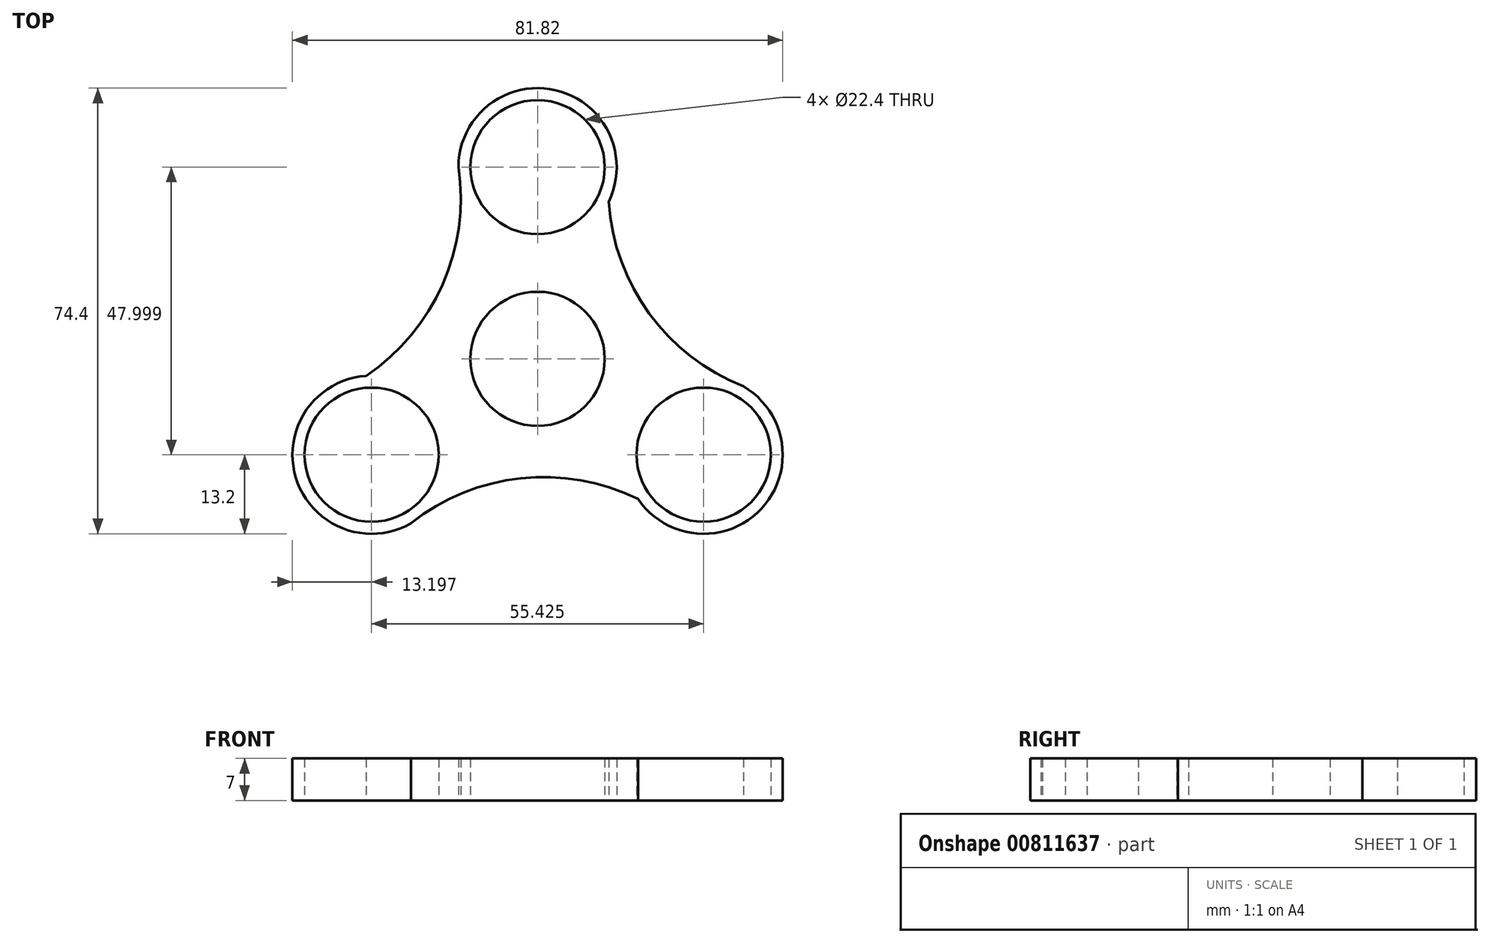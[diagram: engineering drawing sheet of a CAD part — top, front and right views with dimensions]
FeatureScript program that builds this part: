
annotation { "Feature Type Name" : "Feature", "Feature Type Description" : "" }
export const myFeature = defineFeature(function(context is Context, id is Id, definition is map)
    precondition{}
    {
        {
            var Q0;
            Q0=qCreatedBy(makeId("Top.planeOp"),FACE);
            var sketch = newSketch(context, id + "F0", { "sketchPlane" : qUnion([Q0])});
            skCircle(sketch, "E0", {"center": v(0, 0) * mm, "radius": 11.2 * mm});
            skCircle(sketch, "E1", {"center": v(0, 32) * mm, "radius": 11.2 * mm});
            skCircle(sketch, "E2", {"center": v(0, 0) * mm, "radius": 13.2 * mm});
            skCircle(sketch, "E3", {"center": v(0, 32) * mm, "radius": 13.2 * mm});
            skCircle(sketch, "E4.1.0", {"center": v(-27.71, -16) * mm, "radius": 11.2 * mm});
            skCircle(sketch, "E4.1.1", {"center": v(-27.71, -16) * mm, "radius": 13.2 * mm});
            skCircle(sketch, "E4.2.0", {"center": v(27.71, -16) * mm, "radius": 11.2 * mm});
            skCircle(sketch, "E4.2.1", {"center": v(27.71, -16) * mm, "radius": 13.2 * mm});
            skArc(sketch, "E5", {"start": v(-28.63, -2.83) * mm, "mid": v(-15.87, 12.38) * mm, "end": v(-13.2, 32.04) * mm});
            skLineSegment(sketch, "E6", {"start": v(-15.87, 12.38) * mm, "end": v(-9.94, 8.68) * mm});
            skLineSegment(sketch, "E7", {"start": v(-17.08, 9.91) * mm, "end": v(-11.67, 6.17) * mm});
            skArc(sketch, "E8.1.0", {"start": v(16.76, -23.37) * mm, "mid": v(-2.78, -19.93) * mm, "end": v(-21.15, -27.45) * mm});
            skLineSegment(sketch, "E8.1.1", {"start": v(-2.78, -19.93) * mm, "end": v(-2.55, -12.95) * mm});
            skLineSegment(sketch, "E8.1.2", {"start": v(-0.04, -19.75) * mm, "end": v(0.49, -13.2) * mm});
            skArc(sketch, "E8.2.0", {"start": v(11.86, 26.2) * mm, "mid": v(18.65, 7.56) * mm, "end": v(34.35, -4.59) * mm});
            skLineSegment(sketch, "E8.2.1", {"start": v(18.65, 7.56) * mm, "end": v(12.5, 4.27) * mm});
            skLineSegment(sketch, "E8.2.2", {"start": v(17.12, 9.84) * mm, "end": v(11.18, 7.02) * mm});
            skSolve(sketch);
        }
        {
            var Q0;
            Q0=makeQuery(id+"F0.imprint","IMPRINT",FACE,{"disambiguationData":[TD([[makeQuery(id+"F0.imprint","IMPRINT",EDGE,{"derivedFrom":sQuery(id+"F0.wireOp",EDGE,"E1")}),-1.0]])]});
            var Q1;
            Q1=makeQuery(id+"F0.imprint","IMPRINT",FACE,{"disambiguationData":[TD([[makeQuery(id+"F0.imprint","IMPRINT",EDGE,{"derivedFrom":sQuery(id+"F0.wireOp",EDGE,"E4.1.0")}),-1.0]])]});
            var Q2;
            Q2=makeQuery(id+"F0.imprint","IMPRINT",FACE,{"disambiguationData":[TD([[makeQuery(id+"F0.imprint","IMPRINT",EDGE,{"derivedFrom":sQuery(id+"F0.wireOp",EDGE,"E0")}),-1.0]])]});
            var Q3;
            Q3=makeQuery(id+"F0.imprint","IMPRINT",FACE,{"disambiguationData":[TD([[makeQuery(id+"F0.imprint","IMPRINT",EDGE,{"derivedFrom":sQuery(id+"F0.wireOp",EDGE,"E4.2.0")}),-1.0]])]});
            var Q4;
            {var subQ0=sQuery(id+"F0.wireOp",EDGE,"E6");Q4=makeQuery(id+"F0.imprint","IMPRINT",FACE,{"disambiguationData":[TD([[makeQuery(id+"F0.imprint","IMPRINT",EDGE,{"derivedFrom":subQ0}),-1.0]])]});}
            var Q5;
            {var subQ0=sQuery(id+"F0.wireOp",EDGE,"E8.2.1");Q5=makeQuery(id+"F0.imprint","IMPRINT",FACE,{"disambiguationData":[TD([[makeQuery(id+"F0.imprint","IMPRINT",EDGE,{"derivedFrom":subQ0}),-1.0]])]});}
            var Q6;
            {var subQ0=sQuery(id+"F0.wireOp",EDGE,"E8.1.1");Q6=makeQuery(id+"F0.imprint","IMPRINT",FACE,{"disambiguationData":[TD([[makeQuery(id+"F0.imprint","IMPRINT",EDGE,{"derivedFrom":subQ0}),-1.0]])]});}
            var Q7;
            {var subQ0=sQuery(id+"F0.wireOp",EDGE,"E6");Q7=makeQuery(id+"F0.imprint","IMPRINT",FACE,{"disambiguationData":[TD([[makeQuery(id+"F0.imprint","IMPRINT",EDGE,{"derivedFrom":subQ0}),1.0]])]});}
            var Q8;
            {var subQ0=sQuery(id+"F0.wireOp",EDGE,"E7");Q8=makeQuery(id+"F0.imprint","IMPRINT",FACE,{"disambiguationData":[TD([[makeQuery(id+"F0.imprint","IMPRINT",EDGE,{"derivedFrom":subQ0}),-1.0]])]});}
            var Q9;
            {var subQ0=sQuery(id+"F0.wireOp",EDGE,"E8.1.2");Q9=makeQuery(id+"F0.imprint","IMPRINT",FACE,{"disambiguationData":[TD([[makeQuery(id+"F0.imprint","IMPRINT",EDGE,{"derivedFrom":subQ0}),-1.0]])]});}
            extrude(context, id + "F1", {"entities" : qUnion([Q0, Q1, Q2, Q3, Q4, Q5, Q6, Q7, Q8, Q9]), "depth" : 7 * mm, "offsetDistance" : 25 * mm});
        }
    });
